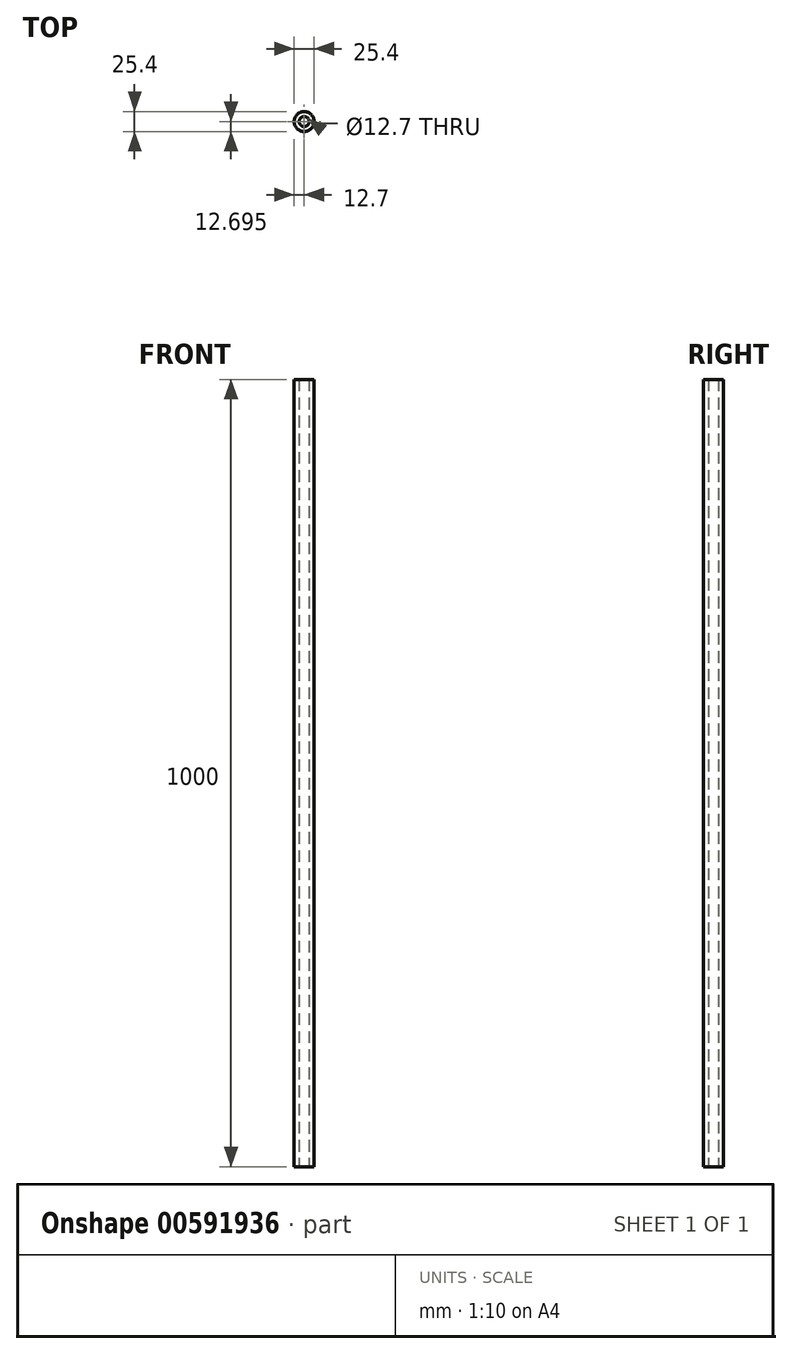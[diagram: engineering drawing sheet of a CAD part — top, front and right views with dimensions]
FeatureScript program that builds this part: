
annotation { "Feature Type Name" : "Feature", "Feature Type Description" : "" }
export const myFeature = defineFeature(function(context is Context, id is Id, definition is map)
    precondition{}
    {
        {
            var Q0;
            Q0=qCreatedBy(makeId("Top.planeOp"),FACE);
            var sketch = newSketch(context, id + "F0", { "sketchPlane" : qUnion([Q0])});
            skCircle(sketch, "E0", {"center": v(0, -3.81) * mm, "radius": 12.7 * mm});
            skCircle(sketch, "E1", {"center": v(0, -3.81) * mm, "radius": 6.35 * mm});
            skSolve(sketch);
        }
        {
            var Q0;
            Q0=makeQuery(id+"F0.imprint","IMPRINT",FACE,{"disambiguationData":[TD([[makeQuery(id+"F0.imprint","IMPRINT",EDGE,{"derivedFrom":sQuery(id+"F0.wireOp",EDGE,"E0")}),1.0]])]});
            extrude(context, id + "F1", {"entities" : qUnion([Q0]), "depth" : 1000 * mm, "offsetDistance" : 25.4 * mm});
        }
    });
